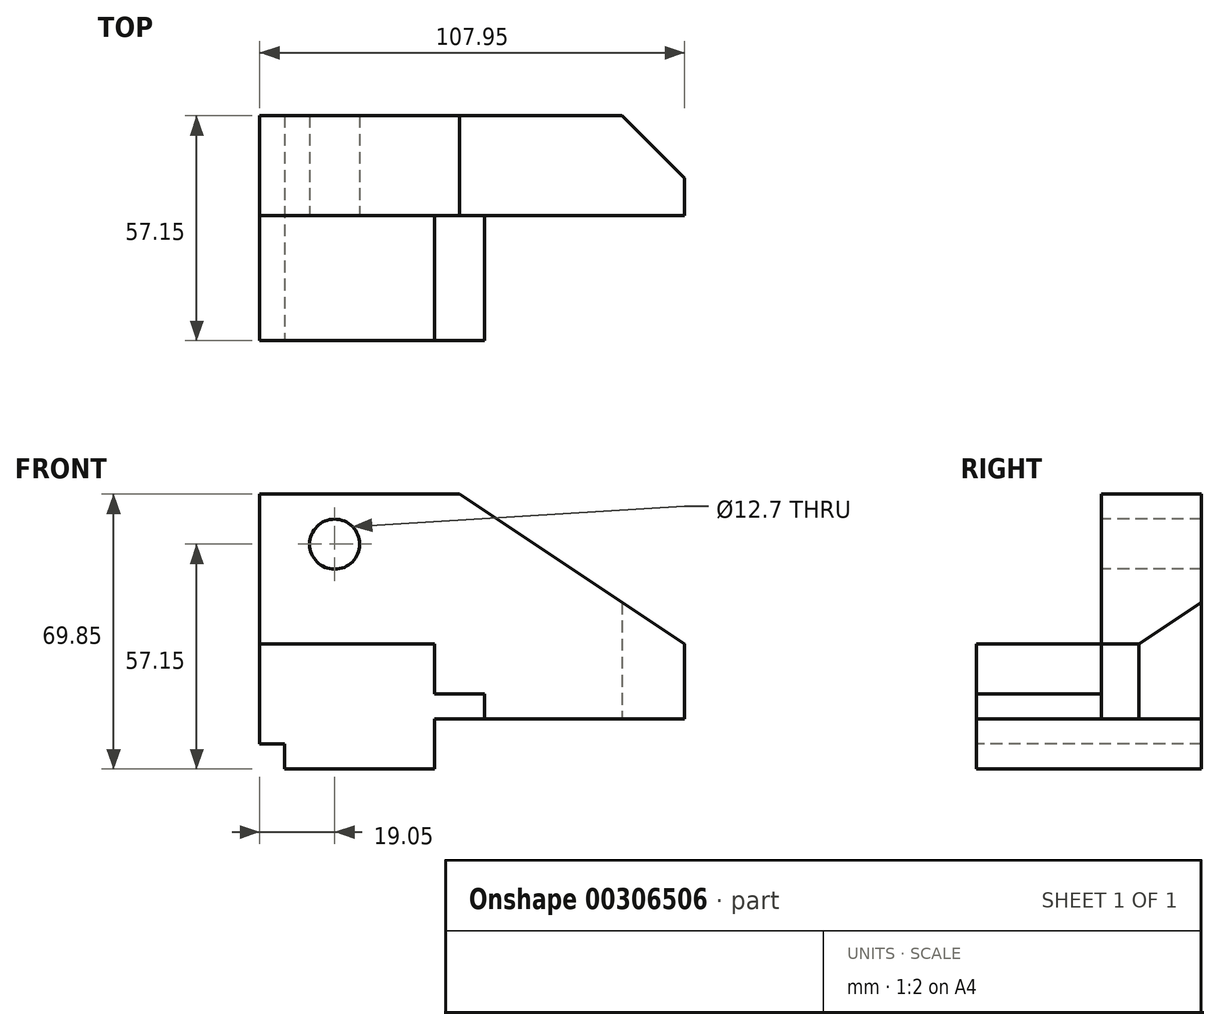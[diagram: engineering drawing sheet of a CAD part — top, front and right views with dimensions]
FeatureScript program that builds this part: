
annotation { "Feature Type Name" : "Feature", "Feature Type Description" : "" }
export const myFeature = defineFeature(function(context is Context, id is Id, definition is map)
    precondition{}
    {
        {
            var Q0;
            Q0=qCreatedBy(makeId("Front.planeOp"),FACE);
            var sketch = newSketch(context, id + "F0", { "sketchPlane" : qUnion([Q0])});
            skLineSegment(sketch, "E0", {"start": v(0, 0) * mm, "end": v(0, 57.15) * mm});
            skLineSegment(sketch, "E1", {"start": v(0, 57.15) * mm, "end": v(50.8, 57.15) * mm});
            skLineSegment(sketch, "E2", {"start": v(0, 0) * mm, "end": v(107.95, 0) * mm});
            skLineSegment(sketch, "E3", {"start": v(107.95, 0) * mm, "end": v(107.95, 19.05) * mm});
            skLineSegment(sketch, "E4", {"start": v(50.8, 57.15) * mm, "end": v(107.95, 19.05) * mm});
            skSolve(sketch);
        }
        {
            var Q0;
            Q0=makeQuery(id+"F0.imprint","IMPRINT",FACE,{"disambiguationData":[TD([[makeQuery(id+"F0.imprint","IMPRINT",EDGE,{"derivedFrom":sQuery(id+"F0.wireOp",EDGE,"E0")}),-1.0]])]});
            extrude(context, id + "F1", {"entities" : qUnion([Q0]), "depth" : 25.4 * mm});
        }
        {
            var Q0;
            Q0=makeQuery(id+"F1.opExtrude","CAP_FACE",FACE,{"disambiguationData":[OSD([sQuery(id+"F0.wireOp",EDGE,"E0"),sQuery(id+"F0.wireOp",EDGE,"E1"),sQuery(id+"F0.wireOp",EDGE,"E2"),sQuery(id+"F0.wireOp",EDGE,"E3"),sQuery(id+"F0.wireOp",EDGE,"E4")])],"isStart":false});
            var sketch = newSketch(context, id + "F2", { "sketchPlane" : qUnion([Q0])});
            skLineSegment(sketch, "E5", {"start": v(0, 0) * mm, "end": v(0, 19.05) * mm});
            skLineSegment(sketch, "E6", {"start": v(0, 0) * mm, "end": v(0, -6.35) * mm});
            skLineSegment(sketch, "E7", {"start": v(0, -6.35) * mm, "end": v(6.35, -6.35) * mm});
            skLineSegment(sketch, "E8", {"start": v(6.35, -6.35) * mm, "end": v(6.35, -12.7) * mm});
            skLineSegment(sketch, "E9", {"start": v(6.35, -12.7) * mm, "end": v(44.45, -12.7) * mm});
            skLineSegment(sketch, "E10", {"start": v(44.45, -12.7) * mm, "end": v(44.45, 0) * mm});
            skLineSegment(sketch, "E11", {"start": v(44.45, 0) * mm, "end": v(57.15, 0) * mm});
            skLineSegment(sketch, "E12", {"start": v(57.15, 0) * mm, "end": v(57.15, 6.35) * mm});
            skLineSegment(sketch, "E13", {"start": v(57.15, 6.35) * mm, "end": v(44.45, 6.35) * mm});
            skLineSegment(sketch, "E14", {"start": v(44.45, 6.35) * mm, "end": v(44.45, 19.05) * mm});
            skLineSegment(sketch, "E15", {"start": v(44.45, 19.05) * mm, "end": v(0, 19.05) * mm});
            skSolve(sketch);
        }
        {
            var Q0;
            {var subQ0=sQuery(id+"F2.wireOp",EDGE,"E6");Q0=makeQuery(id+"F2.imprint","IMPRINT",FACE,{"disambiguationData":[TD([[makeQuery(id+"F2.imprint","IMPRINT",EDGE,{"derivedFrom":subQ0}),1.0]])]});}
            extrude(context, id + "F3", {"entities" : qUnion([Q0]), "operationType" : NewBodyOperationType.ADD, "oppositeDirection" : true, "depth" : 25.4 * mm, "hasSecondDirection" : true, "secondDirectionOppositeDirection" : false, "secondDirectionDepth" : 31.75 * mm});
        }
        {
            var Q0;
            {var subQ1=sQuery(id+"F2.wireOp",EDGE,"E5");Q0=makeQuery(id+"F2.imprint","IMPRINT",FACE,{"disambiguationData":[TD([[makeQuery(id+"F2.imprint","IMPRINT",EDGE,{"derivedFrom":subQ1}),-1.0]])]});}
            extrude(context, id + "F4", {"entities" : qUnion([Q0]), "operationType" : NewBodyOperationType.ADD, "depth" : 31.75 * mm});
        }
        {
            var Q0;
            Q0=makeQuery(id+"F1.opExtrude","CAP_FACE",FACE,{"disambiguationData":[OSD([sQuery(id+"F0.wireOp",EDGE,"E0"),sQuery(id+"F0.wireOp",EDGE,"E1"),sQuery(id+"F0.wireOp",EDGE,"E2"),sQuery(id+"F0.wireOp",EDGE,"E3"),sQuery(id+"F0.wireOp",EDGE,"E4")])],"isStart":false});
            var sketch = newSketch(context, id + "F5", { "sketchPlane" : qUnion([Q0])});
            skCircle(sketch, "E16", {"center": v(19.05, 44.45) * mm, "radius": 6.35 * mm});
            skSolve(sketch);
        }
        {
            var Q0;
            Q0=makeQuery(id+"F5.imprint","IMPRINT",FACE,{"disambiguationData":[TD([[makeQuery(id+"F5.imprint","IMPRINT",EDGE,{"derivedFrom":sQuery(id+"F5.wireOp",EDGE,"E16")}),1.0]])]});
            extrude(context, id + "F6", {"entities" : qUnion([Q0]), "operationType" : NewBodyOperationType.REMOVE, "endBound" : BoundingType.THROUGH_ALL, "oppositeDirection" : true, "depth" : 25.4 * mm});
        }
        {
            var Q0;
            {var subQ0=sQuery(id+"F0.wireOp",EDGE,"E2");Q0=makeQuery(id+"F4.boolean.opBoolean","MERGE",FACE,{"derivedFrom":[makeQuery(id+"F1.opExtrude","SWEPT_FACE",FACE,{"disambiguationData":[OSD([subQ0])]}),makeQuery(id+"F4.opExtrude","SWEPT_FACE",FACE,{"disambiguationData":[OSD([subQ0,sQuery(id+"F2.wireOp",EDGE,"E11")])]})]});}
            var sketch = newSketch(context, id + "F7", { "sketchPlane" : qUnion([Q0])});
            skLineSegment(sketch, "E17", {"start": v(107.95, 15.88) * mm, "end": v(107.95, 0) * mm});
            skLineSegment(sketch, "E18", {"start": v(107.95, 0) * mm, "end": v(92.07, 0) * mm});
            skLineSegment(sketch, "E19", {"start": v(92.07, 0) * mm, "end": v(107.95, 15.87) * mm});
            skSolve(sketch);
        }
        {
            var Q0;
            Q0=makeQuery(id+"F7.imprint","IMPRINT",FACE,{"disambiguationData":[TD([[makeQuery(id+"F7.imprint","IMPRINT",EDGE,{"derivedFrom":sQuery(id+"F7.wireOp",EDGE,"E17")}),-1.0]])]});
            extrude(context, id + "F8", {"entities" : qUnion([Q0]), "operationType" : NewBodyOperationType.REMOVE, "endBound" : BoundingType.THROUGH_ALL, "oppositeDirection" : true, "depth" : 25.4 * mm});
        }
    });
